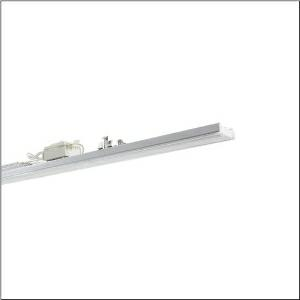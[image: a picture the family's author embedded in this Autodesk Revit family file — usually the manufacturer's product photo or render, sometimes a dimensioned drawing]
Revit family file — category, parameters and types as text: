
# Revit family: licross_r__21_recessed_mo_52te12cn49xg_2497
name_source: partatom
category: Lighting Fixtures
units: mm (PartAtom-declared; Revit-internal decimal feet)

## family parameters
Cut with Voids When Loaded = No
Host = Face
Light Source = No
Part Type = Normal
Room Calculation Point = No
Round Connector Dimension = Use Diameter
Shared = No

## types (1)
- --- (1 x LED, 9260 lm, 49.9 W, 4000K)
    Apparent Load = 50 VA
    CIE Flux Codes = 72 92 99 100 100
    Color Rendering = 80
    Color Temperature = 4000K
    Default Elevation = 1800 mm
    Description = Licross® 21 Recessed MO, luminaire insert, of sheet steel, galvanised, coil coated, white, length: 1.500mm, width: 66mm, height: 67mm, LED rated luminous flux: 9.260lm, light colour: 840, control gear: ON/OFF Multilumen, CLOi, control gear: ECG Multilumen, with plug, 3-pole, with phase selection, mains connection: 220..240V, AC, 50/60Hz, start of lifetime: 49W, end of service life: 61W, halogen-free wiring, primary optical cover: cover, of PMMA, light emission: direct distribution, primary light characteristic: symmetric, protection rating (complete): IP54, insulation class (complete): insulation class I (protective earthing), certification: CE, ENEC, VDE, UKCA, protection symbol: D if used in an environment with non-conductive dust loads with corresponding accessories, impact resistance: IK06, permissible ambient temperature for indoor applications: -35..+40°C, corresponds to IFS (International Featured Standards) requirements for safety and quality in the food industry, reducing of maximum allowable ambient temperature of 5°C with ceiling mounting, LABS conformity tested according to VDMA 24364:2018-05, packaging unit: 1 piece
    Height = 58 mm
    Lamp = 1 x LED
    Lamp Light Flux = 9260 lm
    Lamp Power = 49.9 W
    Lamp count = 1
    Length = 1500 mm
    Luminous efficacy = 186 lm/W
    Manufacturer = Siteco
    ModVariant = No
    Model = 52TE12CN49XG
    Mounting Place = Ceiling
    Mounting Type = Pendant
    Number of Poles = 1
    OnlyDefault = Yes
    Power Factor = 1
    Product Name = Licross® 21 Recessed MO
    Product group = luminaire insert
    ProductGroupID = 902
    Protection Class = Protection class I
    Protection Degree = IP 54
    RLX_Detail_Level = 1
    RLX_Emergency_Light_Flux = 0 lm
    RLX_Emergency_Type = 0
    RLX_Emergency_Type_DB = No
    RlxData = <blob elided: 22337 chars, md5=42d31422>
    Socket = socket
    Standby Power = 0 W
    System Light Flux = 9260 lm
    System Power = 50 W
    Type Comments = factory setting: luminous flux: 100 % | (A | C | E) | 116 mA
    Type Image = l_1296930.jpg
    URL = http://relux.com
    VarID = @adj_110578
    Voltage = 0 V
    Weight = 0.00 kg
    Width = 66 mm

## geometry (parser evidence)
native form markers: Blend x4, Sweep x11
no freeform markers — native parametric forms only
